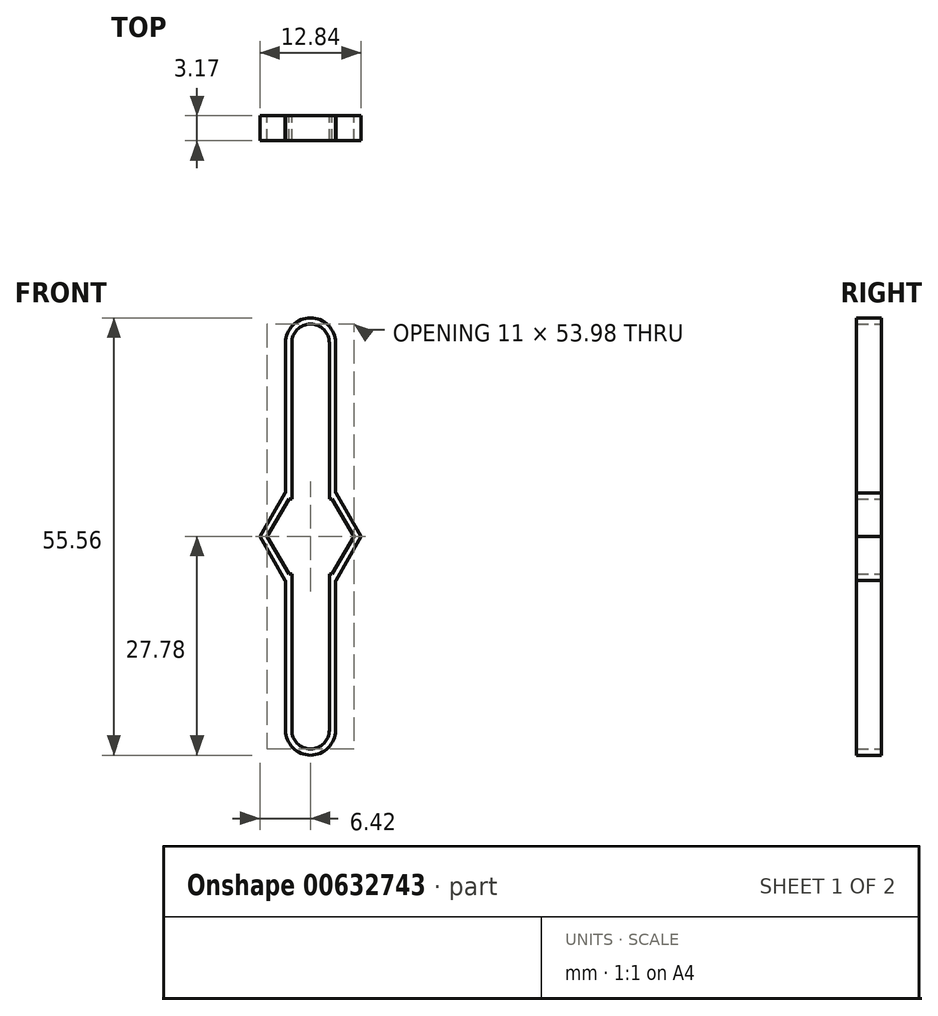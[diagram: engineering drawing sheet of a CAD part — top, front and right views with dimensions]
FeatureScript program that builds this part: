
annotation { "Feature Type Name" : "Feature", "Feature Type Description" : "" }
export const myFeature = defineFeature(function(context is Context, id is Id, definition is map)
    precondition{}
    {
        {
            var Q0;
            Q0=qCreatedBy(makeId("Front.planeOp"),FACE);
            var sketch = newSketch(context, id + "F0", { "sketchPlane" : qUnion([Q0])});
            skLineSegment(sketch, "E0.left", {"start": v(2.38, 24.6) * mm, "end": v(2.38, 4.76) * mm});
            skLineSegment(sketch, "E0.right", {"start": v(-2.38, 24.6) * mm, "end": v(-2.38, 4.76) * mm});
            skPoint(sketch, "E0.middle", {"position": v(0, 0) * mm});
            skArc(sketch, "E1", {"start": v(2.38, 24.6) * mm, "mid": v(0, 26.99) * mm, "end": v(-2.38, 24.6) * mm});
            skArc(sketch, "E2", {"start": v(-2.38, -24.6) * mm, "mid": v(0, -26.99) * mm, "end": v(2.38, -24.6) * mm});
            skCircle(sketch, "E3.cCircle", {"center": v(0, 0) * mm, "radius": 4.76 * mm, "construction": true});
            skLineSegment(sketch, "E3.0", {"start": v(-2.75, -4.76) * mm, "end": v(-5.5, 0) * mm});
            skLineSegment(sketch, "E3.1", {"start": v(-5.5, 0) * mm, "end": v(-2.75, 4.76) * mm});
            skLineSegment(sketch, "E3.2", {"start": v(-2.75, 4.76) * mm, "end": v(2.75, 4.76) * mm});
            skLineSegment(sketch, "E3.3", {"start": v(2.75, 4.76) * mm, "end": v(5.5, 0) * mm});
            skLineSegment(sketch, "E3.4", {"start": v(5.5, 0) * mm, "end": v(2.75, -4.76) * mm});
            skLineSegment(sketch, "E3.5", {"start": v(2.75, -4.76) * mm, "end": v(-2.75, -4.76) * mm});
            skPoint(sketch, "E3.0.midPoint", {"position": v(-4.12, -2.38) * mm});
            skLineSegment(sketch, "E4.trimOffspring", {"start": v(-2.38, -4.76) * mm, "end": v(-2.38, -24.6) * mm});
            skLineSegment(sketch, "E5.trimOffspring", {"start": v(2.38, -4.76) * mm, "end": v(2.38, -24.6) * mm});
            skLineSegment(sketch, "E6.0", {"start": v(3.2, -5.56) * mm, "end": v(-3.2, -5.56) * mm});
            skLineSegment(sketch, "E6.1", {"start": v(-6.42, 0) * mm, "end": v(-3.2, 5.56) * mm});
            skLineSegment(sketch, "E6.2", {"start": v(-3.2, 5.56) * mm, "end": v(3.2, 5.56) * mm});
            skLineSegment(sketch, "E6.3", {"start": v(-3.2, -5.56) * mm, "end": v(-6.42, 0) * mm});
            skLineSegment(sketch, "E6.4", {"start": v(3.2, 5.56) * mm, "end": v(6.42, 0) * mm});
            skLineSegment(sketch, "E6.5", {"start": v(6.42, 0) * mm, "end": v(3.2, -5.56) * mm});
            skLineSegment(sketch, "E7.0", {"start": v(-3.17, 24.6) * mm, "end": v(-3.18, 4.76) * mm});
            skArc(sketch, "E7.1", {"start": v(3.17, 24.6) * mm, "mid": v(0, 27.78) * mm, "end": v(-3.18, 24.6) * mm});
            skLineSegment(sketch, "E7.2", {"start": v(3.18, 24.6) * mm, "end": v(3.17, 4.76) * mm});
            skLineSegment(sketch, "E8.0", {"start": v(3.17, -4.76) * mm, "end": v(3.17, -24.6) * mm});
            skArc(sketch, "E8.1", {"start": v(-3.17, -24.6) * mm, "mid": v(0, -27.78) * mm, "end": v(3.18, -24.6) * mm});
            skLineSegment(sketch, "E8.2", {"start": v(-3.18, -4.76) * mm, "end": v(-3.18, -24.6) * mm});
            skSolve(sketch);
        }
        {
            var Q0;
            {var subQ14=sQuery(id+"F0.wireOp",EDGE,"E3.0");Q0=makeQuery(id+"F0.imprint","IMPRINT",FACE,{"disambiguationData":[TD([[makeQuery(id+"F0.imprint","IMPRINT",EDGE,{"derivedFrom":subQ14}),1.0]])]});}
            var Q1;
            {var subQ13=sQuery(id+"F0.wireOp",EDGE,"E3.3");Q1=makeQuery(id+"F0.imprint","IMPRINT",FACE,{"disambiguationData":[TD([[makeQuery(id+"F0.imprint","IMPRINT",EDGE,{"derivedFrom":subQ13}),1.0]])]});}
            var Q2;
            {var subQ0=sQuery(id+"F0.wireOp",EDGE,"E1");Q2=makeQuery(id+"F0.imprint","IMPRINT",FACE,{"disambiguationData":[TD([[makeQuery(id+"F0.imprint","IMPRINT",EDGE,{"derivedFrom":subQ0}),-1.0]])]});}
            var Q3;
            {var subQ5=sQuery(id+"F0.wireOp",EDGE,"E2");Q3=makeQuery(id+"F0.imprint","IMPRINT",FACE,{"disambiguationData":[TD([[makeQuery(id+"F0.imprint","IMPRINT",EDGE,{"derivedFrom":subQ5}),-1.0]])]});}
            extrude(context, id + "F1", {"entities" : qUnion([Q0, Q1, Q2, Q3]), "depth" : 3.17 * mm, "offsetDistance" : 25.4 * mm});
        }
    });
